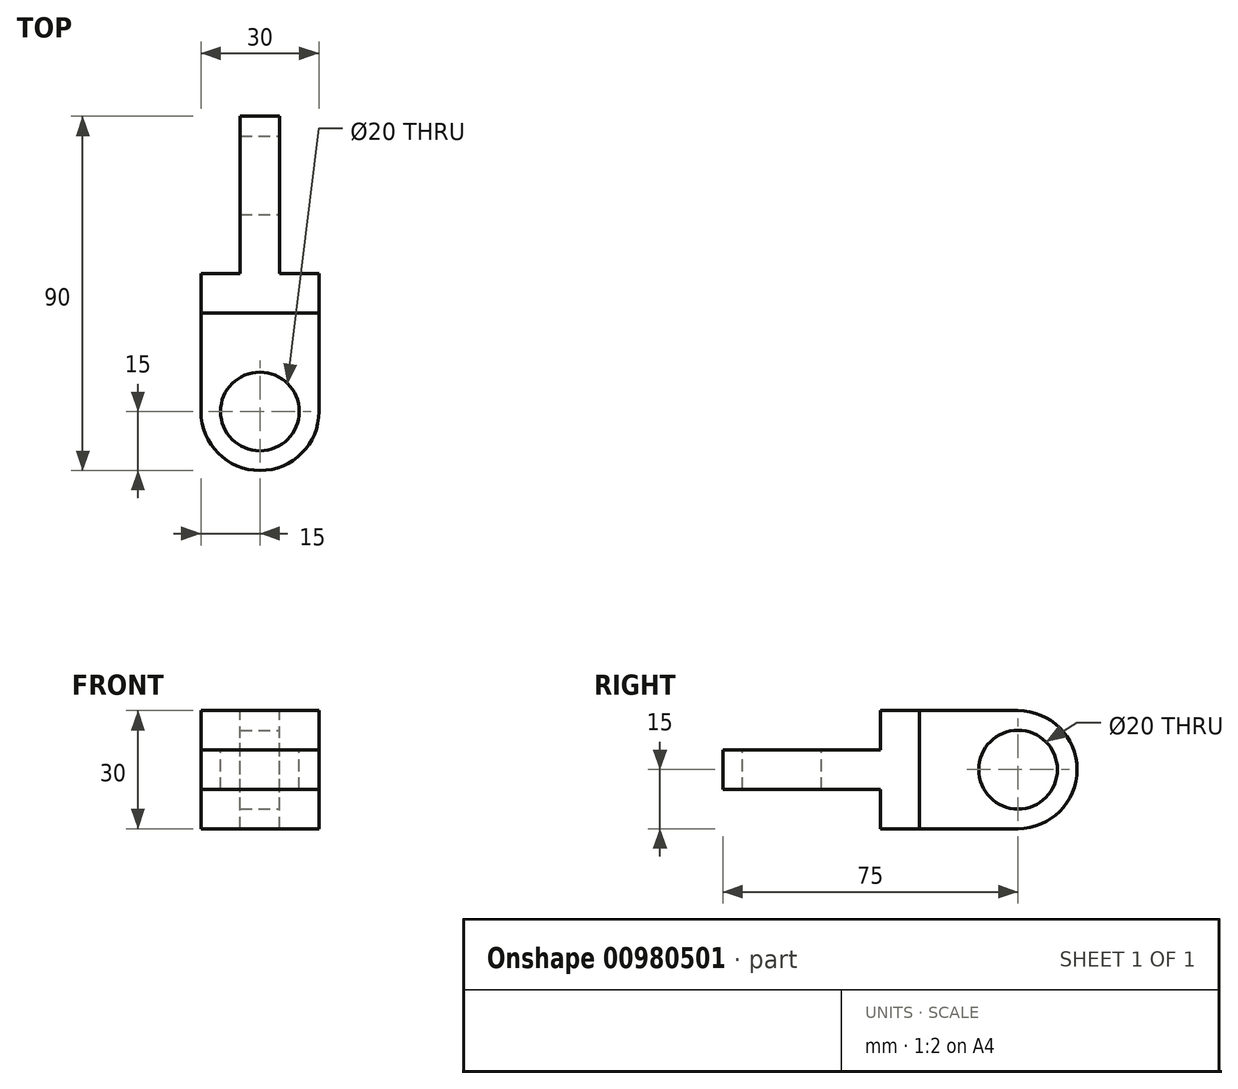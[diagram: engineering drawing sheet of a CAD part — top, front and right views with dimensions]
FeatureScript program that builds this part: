
annotation { "Feature Type Name" : "Feature", "Feature Type Description" : "" }
export const myFeature = defineFeature(function(context is Context, id is Id, definition is map)
    precondition{}
    {
        {
            var Q0;
            Q0=qCreatedBy(makeId("Right.planeOp"),FACE);
            var sketch = newSketch(context, id + "F0", { "sketchPlane" : qUnion([Q0])});
            skLineSegment(sketch, "E0.bottom", {"start": v(5, 15) * mm, "end": v(-5, 15) * mm});
            skLineSegment(sketch, "E0.top", {"start": v(5, -15) * mm, "end": v(-5, -15) * mm});
            skLineSegment(sketch, "E0.left", {"start": v(5, 15) * mm, "end": v(5, -15) * mm});
            skLineSegment(sketch, "E0.right", {"start": v(-5, 15) * mm, "end": v(-5, -15) * mm});
            skPoint(sketch, "E0.middle", {"position": v(0, 0) * mm});
            skSolve(sketch);
        }
        {
            var Q0;
            Q0=makeQuery(id+"F0.imprint","IMPRINT",FACE,{"disambiguationData":[TD([[makeQuery(id+"F0.imprint","IMPRINT",EDGE,{"derivedFrom":sQuery(id+"F0.wireOp",EDGE,"E0.bottom")}),1.0]])]});
            extrude(context, id + "F1", {"entities" : qUnion([Q0]), "endBound" : BoundingType.SYMMETRIC, "depth" : 30 * mm, "offsetDistance" : 25 * mm});
        }
        {
            var Q0;
            Q0=makeQuery(id+"F1.opExtrude","SWEPT_FACE",FACE,{"disambiguationData":[OSD([sQuery(id+"F0.wireOp",EDGE,"E0.right")])]});
            var sketch = newSketch(context, id + "F2", { "sketchPlane" : qUnion([Q0])});
            skLineSegment(sketch, "E1.bottom", {"start": v(15, 5) * mm, "end": v(-15, 5) * mm});
            skLineSegment(sketch, "E1.top", {"start": v(15, -5) * mm, "end": v(-15, -5) * mm});
            skLineSegment(sketch, "E1.left", {"start": v(15, 5) * mm, "end": v(15, -5) * mm});
            skLineSegment(sketch, "E1.right", {"start": v(-15, 5) * mm, "end": v(-15, -5) * mm});
            skPoint(sketch, "E1.middle", {"position": v(0, 0) * mm});
            skSolve(sketch);
        }
        {
            var Q0;
            Q0 = qSketchRegion(id + "F2", true);
            extrude(context, id + "F3", {"entities" : qUnion([Q0]), "operationType" : NewBodyOperationType.ADD, "depth" : 40 * mm, "offsetDistance" : 25 * mm});
        }
        {
            var Q0;
            Q0=makeQuery(id+"F3.opExtrude","CAP_EDGE",EDGE,{"disambiguationData":[OSD([sQuery(id+"F2.wireOp",EDGE,"E1.right")])],"isStart":false});
            var Q1;
            Q1=makeQuery(id+"F3.opExtrude","CAP_EDGE",EDGE,{"disambiguationData":[OSD([sQuery(id+"F2.wireOp",EDGE,"E1.left")])],"isStart":false});
            fillet(context, id + "F4", {"entities" : qUnion([Q0, Q1]), "radius" : 15 * mm, "tangentPropagation" : true, "allowEdgeOverflow" : false});
        }
        {
            var Q0;
            Q0=makeQuery(id+"F1.opExtrude","SWEPT_FACE",FACE,{"disambiguationData":[OSD([sQuery(id+"F0.wireOp",EDGE,"E0.left")])]});
            var sketch = newSketch(context, id + "F5", { "sketchPlane" : qUnion([Q0])});
            skLineSegment(sketch, "E2.bottom", {"start": v(5, -15) * mm, "end": v(-5, -15) * mm});
            skLineSegment(sketch, "E2.top", {"start": v(5, 15) * mm, "end": v(-5, 15) * mm});
            skLineSegment(sketch, "E2.left", {"start": v(5, -15) * mm, "end": v(5, 15) * mm});
            skLineSegment(sketch, "E2.right", {"start": v(-5, -15) * mm, "end": v(-5, 15) * mm});
            skPoint(sketch, "E2.middle", {"position": v(0, 0) * mm});
            skSolve(sketch);
        }
        {
            var Q0;
            Q0=makeQuery(id+"F5.imprint","IMPRINT",FACE,{"disambiguationData":[TD([[makeQuery(id+"F5.imprint","IMPRINT",EDGE,{"derivedFrom":sQuery(id+"F5.wireOp",EDGE,"E2.bottom")}),1.0]])]});
            extrude(context, id + "F6", {"entities" : qUnion([Q0]), "operationType" : NewBodyOperationType.ADD, "depth" : 40 * mm, "offsetDistance" : 25 * mm});
        }
        {
            var Q0;
            Q0=makeQuery(id+"F6.opExtrude","CAP_EDGE",EDGE,{"disambiguationData":[OSD([sQuery(id+"F5.wireOp",EDGE,"E2.top")])],"isStart":false});
            var Q1;
            Q1=makeQuery(id+"F6.opExtrude","CAP_EDGE",EDGE,{"disambiguationData":[OSD([sQuery(id+"F5.wireOp",EDGE,"E2.bottom")])],"isStart":false});
            fillet(context, id + "F7", {"entities" : qUnion([Q0, Q1]), "radius" : 15 * mm, "tangentPropagation" : true, "allowEdgeOverflow" : false});
        }
        {
            var Q0;
            Q0=makeQuery(id+"F3.opExtrude","SWEPT_FACE",FACE,{"disambiguationData":[OSD([sQuery(id+"F2.wireOp",EDGE,"E1.bottom")])]});
            var sketch = newSketch(context, id + "F8", { "sketchPlane" : qUnion([Q0])});
            skCircle(sketch, "E3", {"center": v(0, -30) * mm, "radius": 10 * mm});
            skSolve(sketch);
        }
        {
            var Q0;
            Q0=makeQuery(id+"F8.imprint","IMPRINT",FACE,{"disambiguationData":[TD([[makeQuery(id+"F8.imprint","IMPRINT",EDGE,{"derivedFrom":sQuery(id+"F8.wireOp",EDGE,"E3")}),1.0]])]});
            extrude(context, id + "F9", {"entities" : qUnion([Q0]), "operationType" : NewBodyOperationType.REMOVE, "endBound" : BoundingType.UP_TO_NEXT, "oppositeDirection" : true, "depth" : 25 * mm, "offsetDistance" : 25 * mm});
        }
        {
            var Q0;
            Q0=makeQuery(id+"F6.opExtrude","SWEPT_FACE",FACE,{"disambiguationData":[OSD([sQuery(id+"F5.wireOp",EDGE,"E2.right")])]});
            var sketch = newSketch(context, id + "F10", { "sketchPlane" : qUnion([Q0])});
            skCircle(sketch, "E4", {"center": v(30, 0) * mm, "radius": 10 * mm});
            skSolve(sketch);
        }
        {
            var Q0;
            Q0=makeQuery(id+"F10.imprint","IMPRINT",FACE,{"disambiguationData":[TD([[makeQuery(id+"F10.imprint","IMPRINT",EDGE,{"derivedFrom":sQuery(id+"F10.wireOp",EDGE,"E4")}),1.0]])]});
            extrude(context, id + "F11", {"entities" : qUnion([Q0]), "operationType" : NewBodyOperationType.REMOVE, "endBound" : BoundingType.UP_TO_NEXT, "oppositeDirection" : true, "depth" : 25 * mm, "offsetDistance" : 25 * mm});
        }
    });
